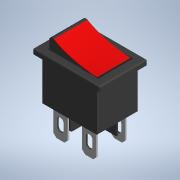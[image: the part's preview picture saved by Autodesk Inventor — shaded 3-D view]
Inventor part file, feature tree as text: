
AUTODESK INVENTOR PART (.ipt)
format: ipt  version: 2022 (Build 260153000, 153)  size: 241,152 bytes
history: native  units: mm (DEFAULTED — no unit token found)
features: other x8, projected_geometry x4, extrude x2, sketch x2, imported_body x1
bodies: Body1 (feature_tree)
feature tree (17):
  other  "Sólido1"
  other  "Origen"
  extrude  "Extrusión1"  Depth=10.0mm TaperAngle=0.0deg
  extrude  "Extrusión2"  [1 undecoded]
  other  "Plano YZ"
  other  "Plano XZ"
  other  "Plano XY"
  other  "Eje X"
  other  "Eje Y"
  other  "Eje Z"
  sketch  "Boceto1"  dims[d0=10.0mm d1=0.0mm d2=10.0mm d3=0.0mm]
  projected_geometry  "Contorno proyectado1"
  projected_geometry  "Contorno proyectado2"
  sketch  "Boceto2"
  projected_geometry  "Contorno proyectado3"
  projected_geometry  "Contorno proyectado4"
  imported_body  "Imported1"
note: 1 required parameter value undecoded (feature->parameter linkage not recoverable at this tier; creation-order binding heuristic only, values carry confidence <= 0.55)
